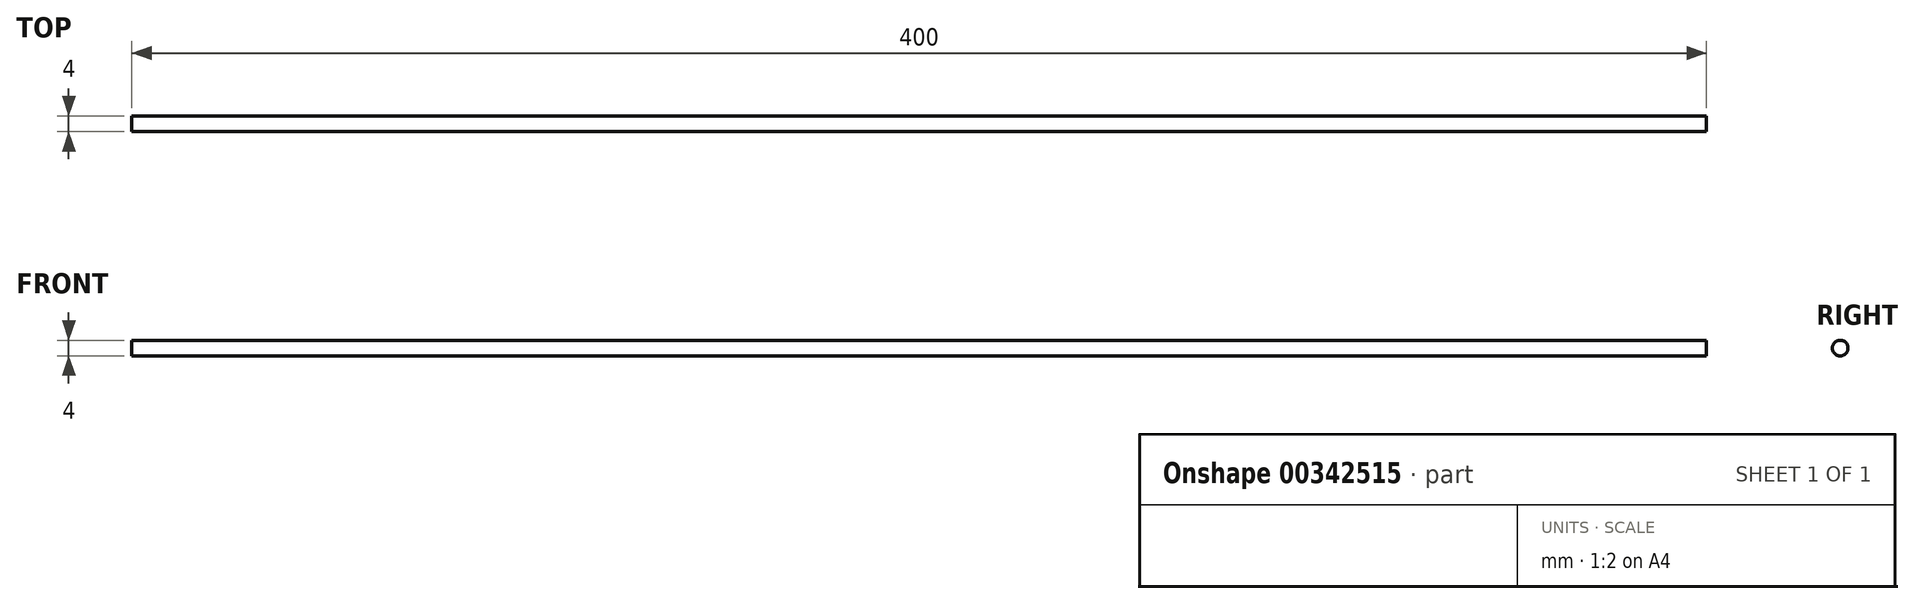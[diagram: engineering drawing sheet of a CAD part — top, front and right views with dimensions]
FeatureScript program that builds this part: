
annotation { "Feature Type Name" : "Feature", "Feature Type Description" : "" }
export const myFeature = defineFeature(function(context is Context, id is Id, definition is map)
    precondition{}
    {
        {
            var Q0;
            Q0=qCreatedBy(makeId("Right.planeOp"),FACE);
            var sketch = newSketch(context, id + "F0", { "sketchPlane" : qUnion([Q0])});
            skCircle(sketch, "E0", {"center": v(0, 0) * mm, "radius": 2 * mm});
            skSolve(sketch);
        }
        {
            var Q0;
            Q0=makeQuery(id+"F0.imprint","IMPRINT",FACE,{"disambiguationData":[TD([[makeQuery(id+"F0.imprint","IMPRINT",EDGE,{"derivedFrom":sQuery(id+"F0.wireOp",EDGE,"E0")}),1.0]])]});
            extrude(context, id + "F1", {"entities" : qUnion([Q0]), "depth" : 400 * mm});
        }
    });
